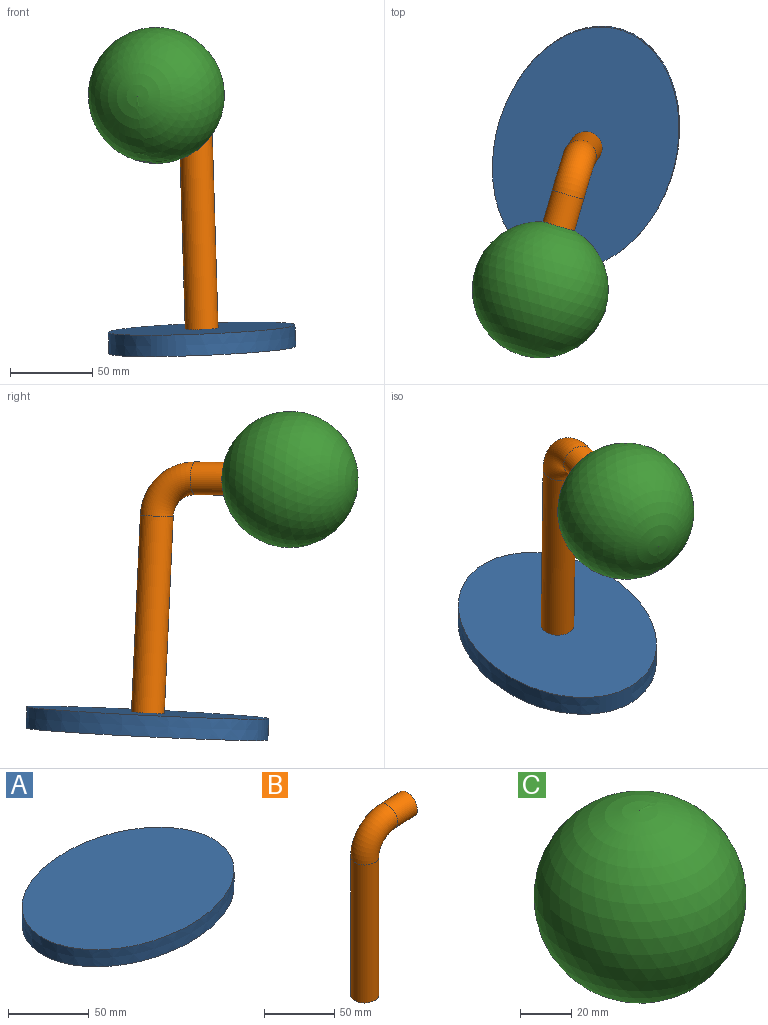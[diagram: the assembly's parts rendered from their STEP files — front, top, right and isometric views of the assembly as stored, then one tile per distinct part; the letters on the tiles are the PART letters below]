
ASSEMBLY  parts=3 mates=2
PART A: 3 faces, bbox 150x110x13 mm
  f0: plane 150x110mm, normal (0,0,-1), area 12972.2mm2, adj f1
  f1: extruded ~150x110mm, area 5343.4mm2, adj f0,f2
  f2: plane 150x110mm, normal (0,0,1), area 12972.2mm2, adj f1
PART B: 5 faces, bbox 56.2x20x156.8 mm
  f0: plane 20x19.98mm, normal (1,0,0.04), area 314.2mm2, adj f3
  f1: cylinder r=10mm len=120mm, axis (0,0,1), area 7539.8mm2, adj f2,f4
  f2: torus R=24mm, axis (0,1,0), area 2307.5mm2, adj f1,f3
  f3: cylinder r=10mm len=20.79mm, axis (1,0,0.04), area 1256.6mm2, adj f0,f2
  f4: plane 20x20mm, normal (0,0,-1), area 314.2mm2, adj f1
PART C: 3 faces, bbox 82.9x82.9x81.7 mm
  f0: sphere r=41.47mm, area 21294.3mm2, adj f1
  f1: cylinder r=10mm len=40.25mm, axis (0,0,1), area 2528.9mm2, adj f0,f2
  f2: plane 20x20mm, normal (0,0,-1), area 314.2mm2, adj f1
PLACE A rot(axis=(0.03,0.01,-1),106.2deg) t=(-21.35,205.43,-254.63)mm
PLACE B rot(axis=(0.03,0.01,-1),106.2deg) t=(-24.77,200.32,-141.8)mm
PLACE C rot(axis=(0.63,0.47,-0.62),129.5deg) t=(-49.34,118.4,-99.76)mm
MATE fastened C.f1 <-> B.f3  axis (-0.28,-0.96,-0.01) through (-38.1,157.04,-99.31)mm
MATE fastened B.f1 <-> A.f2  axis (0.03,0.05,-1) through (-21.74,204.84,-241.65)mm
